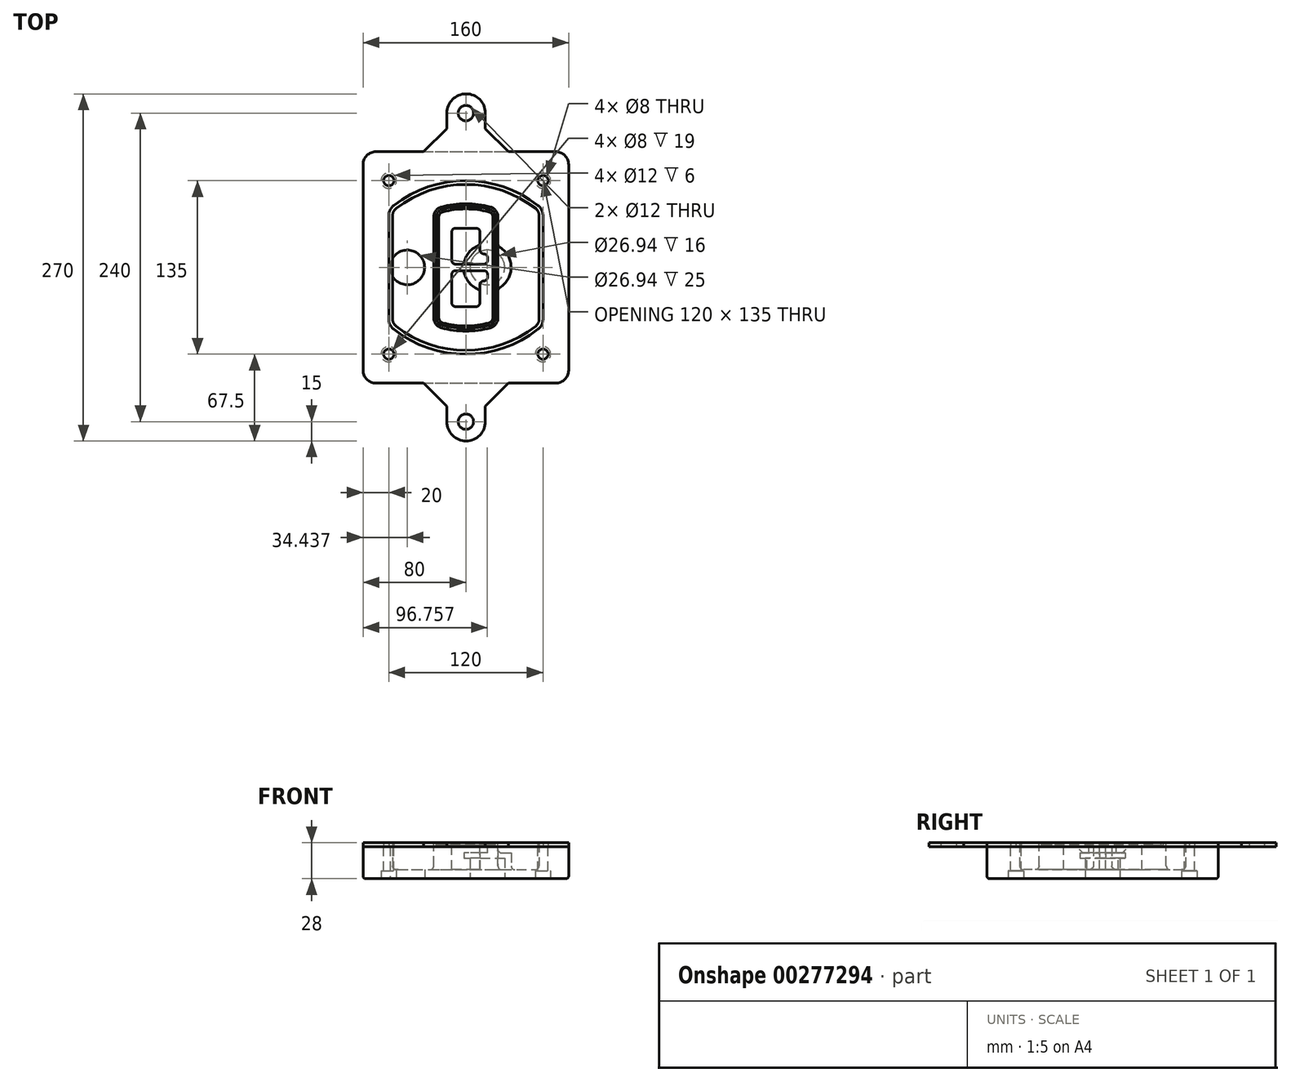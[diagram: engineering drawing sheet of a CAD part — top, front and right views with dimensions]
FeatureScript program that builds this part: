
annotation { "Feature Type Name" : "Feature", "Feature Type Description" : "" }
export const myFeature = defineFeature(function(context is Context, id is Id, definition is map)
    precondition{}
    {
        {
            var Q0;
            Q0=qCreatedBy(makeId("Top.planeOp"),FACE);
            var sketch = newSketch(context, id + "F0", { "sketchPlane" : qUnion([Q0])});
            skPoint(sketch, "E0.rect.middle", {"position": v(0, 0) * mm});
            skLineSegment(sketch, "E1.bottom", {"start": v(-70, -90) * mm, "end": v(70, -90) * mm});
            skLineSegment(sketch, "E1.top", {"start": v(-70, 90) * mm, "end": v(70, 90) * mm});
            skLineSegment(sketch, "E1.left", {"start": v(-80, -80) * mm, "end": v(-80, 80) * mm});
            skLineSegment(sketch, "E1.right", {"start": v(80, -80) * mm, "end": v(80, 80) * mm});
            skLineSegment(sketch, "E2", {"start": v(-80, 90) * mm, "end": v(80, -90) * mm, "construction": true});
            skLineSegment(sketch, "E3", {"start": v(80, 90) * mm, "end": v(-80, -90) * mm, "construction": true});
            skCircle(sketch, "E4", {"center": v(-60, 67.5) * mm, "radius": 4 * mm});
            skCircle(sketch, "E5", {"center": v(60, 67.5) * mm, "radius": 4 * mm});
            skCircle(sketch, "E6", {"center": v(60, -67.5) * mm, "radius": 4 * mm});
            skCircle(sketch, "E7", {"center": v(-60, -67.5) * mm, "radius": 4 * mm});
            skLineSegment(sketch, "E8", {"start": v(-60, 67.5) * mm, "end": v(60, 67.5) * mm, "construction": true});
            skLineSegment(sketch, "E9", {"start": v(60, 67.5) * mm, "end": v(60, -67.5) * mm, "construction": true});
            skLineSegment(sketch, "E10", {"start": v(60, -67.5) * mm, "end": v(-60, -67.5) * mm, "construction": true});
            skLineSegment(sketch, "E11", {"start": v(-60, -67.5) * mm, "end": v(-60, 67.5) * mm, "construction": true});
            skLineSegment(sketch, "E12", {"start": v(-60, 40.3) * mm, "end": v(-60, -40.3) * mm});
            skLineSegment(sketch, "E13", {"start": v(60, 40.3) * mm, "end": v(60, -40.3) * mm});
            skArc(sketch, "E14", {"start": v(56.15, 48.18) * mm, "mid": v(0, 67.5) * mm, "end": v(-56.15, 48.18) * mm});
            skArc(sketch, "E15", {"start": v(-56.15, -48.18) * mm, "mid": v(0, -67.5) * mm, "end": v(56.15, -48.18) * mm});
            skLineSegment(sketch, "E16", {"start": v(-60, 0) * mm, "end": v(60, 0) * mm, "construction": true});
            skPoint(sketch, "E17.visualSharp", {"position": v(-60, -45) * mm});
            skArc(sketch, "E17.filletArc", {"start": v(-60, -40.3) * mm, "mid": v(-58.99, -44.68) * mm, "end": v(-56.15, -48.18) * mm});
            skPoint(sketch, "E18.visualSharp", {"position": v(-60, 45) * mm});
            skArc(sketch, "E18.filletArc", {"start": v(-56.15, 48.18) * mm, "mid": v(-58.99, 44.68) * mm, "end": v(-60, 40.3) * mm});
            skPoint(sketch, "E19.visualSharp", {"position": v(60, 45) * mm});
            skArc(sketch, "E19.filletArc", {"start": v(60, 40.3) * mm, "mid": v(58.99, 44.68) * mm, "end": v(56.15, 48.18) * mm});
            skPoint(sketch, "E20.visualSharp", {"position": v(60, -45) * mm});
            skArc(sketch, "E20.filletArc", {"start": v(56.15, -48.18) * mm, "mid": v(58.99, -44.68) * mm, "end": v(60, -40.3) * mm});
            skPoint(sketch, "E21.visualSharp", {"position": v(-80, 90) * mm});
            skArc(sketch, "E21.filletArc", {"start": v(-70, 90) * mm, "mid": v(-77.07, 87.07) * mm, "end": v(-80, 80) * mm});
            skPoint(sketch, "E22.visualSharp", {"position": v(80, 90) * mm});
            skArc(sketch, "E22.filletArc", {"start": v(80, 80) * mm, "mid": v(77.07, 87.07) * mm, "end": v(70, 90) * mm});
            skPoint(sketch, "E23.visualSharp", {"position": v(80, -90) * mm});
            skArc(sketch, "E23.filletArc", {"start": v(70, -90) * mm, "mid": v(77.07, -87.07) * mm, "end": v(80, -80) * mm});
            skPoint(sketch, "E24.visualSharp", {"position": v(-80, -90) * mm});
            skArc(sketch, "E24.filletArc", {"start": v(-80, -80) * mm, "mid": v(-77.07, -87.07) * mm, "end": v(-70, -90) * mm});
            skArc(sketch, "E25.0", {"start": v(57, 40.3) * mm, "mid": v(56.3, 43.36) * mm, "end": v(54.3, 45.81) * mm});
            skLineSegment(sketch, "E25.1", {"start": v(57, 40.3) * mm, "end": v(57, -40.3) * mm});
            skArc(sketch, "E25.2", {"start": v(54.3, -45.81) * mm, "mid": v(56.3, -43.36) * mm, "end": v(57, -40.3) * mm});
            skArc(sketch, "E25.3", {"start": v(-54.3, -45.81) * mm, "mid": v(0, -64.5) * mm, "end": v(54.3, -45.81) * mm});
            skArc(sketch, "E25.4", {"start": v(-57, -40.3) * mm, "mid": v(-56.3, -43.36) * mm, "end": v(-54.3, -45.81) * mm});
            skArc(sketch, "E25.5", {"start": v(54.3, 45.81) * mm, "mid": v(0, 64.5) * mm, "end": v(-54.3, 45.81) * mm});
            skLineSegment(sketch, "E25.6", {"start": v(-57, 40.3) * mm, "end": v(-57, -40.3) * mm});
            skArc(sketch, "E25.7", {"start": v(-54.3, 45.81) * mm, "mid": v(-56.3, 43.36) * mm, "end": v(-57, 40.3) * mm});
            skArc(sketch, "E26.0", {"start": v(-58.62, 51.33) * mm, "mid": v(-62.58, 46.43) * mm, "end": v(-64, 40.3) * mm});
            skArc(sketch, "E26.1", {"start": v(58.62, 51.33) * mm, "mid": v(0, 71.5) * mm, "end": v(-58.62, 51.33) * mm});
            skArc(sketch, "E26.2", {"start": v(64, 40.3) * mm, "mid": v(62.58, 46.43) * mm, "end": v(58.62, 51.33) * mm});
            skLineSegment(sketch, "E26.3", {"start": v(64, 40.3) * mm, "end": v(64, -40.3) * mm});
            skArc(sketch, "E26.4", {"start": v(58.62, -51.33) * mm, "mid": v(62.58, -46.43) * mm, "end": v(64, -40.3) * mm});
            skLineSegment(sketch, "E26.5", {"start": v(-64, 40.3) * mm, "end": v(-64, -40.3) * mm});
            skArc(sketch, "E26.6", {"start": v(-58.62, -51.33) * mm, "mid": v(0, -71.5) * mm, "end": v(58.62, -51.33) * mm});
            skArc(sketch, "E26.7", {"start": v(-64, -40.3) * mm, "mid": v(-62.58, -46.43) * mm, "end": v(-58.62, -51.33) * mm});
            skSolve(sketch);
        }
        {
            var Q0;
            Q0=makeQuery(id+"F0.imprint","IMPRINT",FACE,{"disambiguationData":[TD([[makeQuery(id+"F0.imprint","IMPRINT",EDGE,{"derivedFrom":sQuery(id+"F0.wireOp",EDGE,"E1.bottom")}),1.0]])]});
            var Q1;
            Q1=makeQuery(id+"F0.imprint","IMPRINT",FACE,{"disambiguationData":[TD([[makeQuery(id+"F0.imprint","IMPRINT",EDGE,{"derivedFrom":sQuery(id+"F0.wireOp",EDGE,"E12")}),1.0]])]});
            var Q2;
            Q2=makeQuery(id+"F0.imprint","IMPRINT",FACE,{"disambiguationData":[TD([[makeQuery(id+"F0.imprint","IMPRINT",EDGE,{"derivedFrom":sQuery(id+"F0.wireOp",EDGE,"E25.0")}),1.0]])]});
            var Q3;
            Q3=makeQuery(id+"F0.imprint","IMPRINT",FACE,{"disambiguationData":[TD([[makeQuery(id+"F0.imprint","IMPRINT",EDGE,{"derivedFrom":sQuery(id+"F0.wireOp",EDGE,"E12")}),-1.0]])]});
            extrude(context, id + "F1", {"entities" : qUnion([Q0, Q1, Q2, Q3]), "oppositeDirection" : true, "depth" : 25 * mm});
        }
        {
            var Q0;
            Q0=makeQuery(id+"F0.imprint","IMPRINT",FACE,{"disambiguationData":[TD([[makeQuery(id+"F0.imprint","IMPRINT",EDGE,{"derivedFrom":sQuery(id+"F0.wireOp",EDGE,"E12")}),1.0]])]});
            extrude(context, id + "F2", {"entities" : qUnion([Q0]), "operationType" : NewBodyOperationType.ADD, "depth" : 3 * mm});
        }
        {
            var Q0;
            Q0=makeQuery(id+"F0.imprint","IMPRINT",FACE,{"disambiguationData":[TD([[makeQuery(id+"F0.imprint","IMPRINT",EDGE,{"derivedFrom":sQuery(id+"F0.wireOp",EDGE,"E25.0")}),1.0]])]});
            extrude(context, id + "F3", {"entities" : qUnion([Q0]), "operationType" : NewBodyOperationType.REMOVE, "oppositeDirection" : true, "depth" : 18 * mm});
        }
        {
            var Q0;
            Q0=makeQuery(id+"F2.opExtrude","CAP_FACE",FACE,{"disambiguationData":[OSD([sQuery(id+"F0.wireOp",EDGE,"E12"),sQuery(id+"F0.wireOp",EDGE,"E13"),sQuery(id+"F0.wireOp",EDGE,"E14"),sQuery(id+"F0.wireOp",EDGE,"E15"),sQuery(id+"F0.wireOp",EDGE,"E17.filletArc"),sQuery(id+"F0.wireOp",EDGE,"E18.filletArc"),sQuery(id+"F0.wireOp",EDGE,"E19.filletArc"),sQuery(id+"F0.wireOp",EDGE,"E20.filletArc"),sQuery(id+"F0.wireOp",EDGE,"E25.0"),sQuery(id+"F0.wireOp",EDGE,"E25.1"),sQuery(id+"F0.wireOp",EDGE,"E25.2"),sQuery(id+"F0.wireOp",EDGE,"E25.3"),sQuery(id+"F0.wireOp",EDGE,"E25.4"),sQuery(id+"F0.wireOp",EDGE,"E25.5"),sQuery(id+"F0.wireOp",EDGE,"E25.6"),sQuery(id+"F0.wireOp",EDGE,"E25.7")])],"isStart":false});
            var sketch = newSketch(context, id + "F4", { "sketchPlane" : qUnion([Q0])});
            skArc(sketch, "E27.0", {"start": v(-19.08, -46.97) * mm, "mid": v(0, -49.5) * mm, "end": v(19.08, -46.97) * mm});
            skArc(sketch, "E28.0", {"start": v(19.08, 46.97) * mm, "mid": v(0, 49.5) * mm, "end": v(-19.08, 46.97) * mm});
            skLineSegment(sketch, "E29", {"start": v(-25, 39.25) * mm, "end": v(-25, -39.25) * mm});
            skLineSegment(sketch, "E30", {"start": v(25, 39.25) * mm, "end": v(25, -39.25) * mm});
            skLineSegment(sketch, "E31", {"start": v(-25, 45.1) * mm, "end": v(25, 45.1) * mm, "construction": true});
            skLineSegment(sketch, "E32", {"start": v(-25, -45.1) * mm, "end": v(25, -45.1) * mm, "construction": true});
            skPoint(sketch, "E33.visualSharp", {"position": v(-25, 45.1) * mm});
            skArc(sketch, "E33.filletArc", {"start": v(-19.08, 46.97) * mm, "mid": v(-23.35, 44.11) * mm, "end": v(-25, 39.25) * mm});
            skPoint(sketch, "E34.visualSharp", {"position": v(25, 45.1) * mm});
            skArc(sketch, "E34.filletArc", {"start": v(25, 39.25) * mm, "mid": v(23.35, 44.11) * mm, "end": v(19.08, 46.97) * mm});
            skPoint(sketch, "E35.visualSharp", {"position": v(25, -45.1) * mm});
            skArc(sketch, "E35.filletArc", {"start": v(19.08, -46.97) * mm, "mid": v(23.35, -44.11) * mm, "end": v(25, -39.25) * mm});
            skPoint(sketch, "E36.visualSharp", {"position": v(-25, -45.1) * mm});
            skArc(sketch, "E36.filletArc", {"start": v(-25, -39.25) * mm, "mid": v(-23.35, -44.11) * mm, "end": v(-19.08, -46.97) * mm});
            skArc(sketch, "E37.0", {"start": v(54.3, 45.81) * mm, "mid": v(0, 64.5) * mm, "end": v(-54.3, 45.81) * mm});
            skArc(sketch, "E37.1", {"start": v(-54.3, 45.81) * mm, "mid": v(-56.3, 43.36) * mm, "end": v(-57, 40.3) * mm});
            skLineSegment(sketch, "E37.2", {"start": v(-57, 40.3) * mm, "end": v(-57, -40.3) * mm});
            skArc(sketch, "E37.3", {"start": v(-57, -40.3) * mm, "mid": v(-56.3, -43.36) * mm, "end": v(-54.3, -45.81) * mm});
            skArc(sketch, "E37.4", {"start": v(-54.3, -45.81) * mm, "mid": v(0, -64.5) * mm, "end": v(54.3, -45.81) * mm});
            skArc(sketch, "E37.5", {"start": v(54.3, -45.81) * mm, "mid": v(56.3, -43.36) * mm, "end": v(57, -40.3) * mm});
            skLineSegment(sketch, "E37.6", {"start": v(57, 40.3) * mm, "end": v(57, -40.3) * mm});
            skArc(sketch, "E37.7", {"start": v(57, 40.3) * mm, "mid": v(56.3, 43.36) * mm, "end": v(54.3, 45.81) * mm});
            skLineSegment(sketch, "E38.0", {"start": v(23, 39.25) * mm, "end": v(23, -39.25) * mm});
            skArc(sketch, "E38.1", {"start": v(18.56, -45.04) * mm, "mid": v(21.76, -42.9) * mm, "end": v(23, -39.25) * mm});
            skArc(sketch, "E38.2", {"start": v(-18.56, -45.04) * mm, "mid": v(0, -47.5) * mm, "end": v(18.56, -45.04) * mm});
            skArc(sketch, "E38.3", {"start": v(-23, -39.25) * mm, "mid": v(-21.76, -42.9) * mm, "end": v(-18.56, -45.04) * mm});
            skLineSegment(sketch, "E38.4", {"start": v(-23, 39.25) * mm, "end": v(-23, -39.25) * mm});
            skArc(sketch, "E38.5", {"start": v(23, 39.25) * mm, "mid": v(21.76, 42.9) * mm, "end": v(18.56, 45.04) * mm});
            skArc(sketch, "E38.6", {"start": v(-18.56, 45.04) * mm, "mid": v(-21.76, 42.9) * mm, "end": v(-23, 39.25) * mm});
            skArc(sketch, "E38.7", {"start": v(18.56, 45.04) * mm, "mid": v(0, 47.5) * mm, "end": v(-18.56, 45.04) * mm});
            skArc(sketch, "E39.0", {"start": v(21, 39.25) * mm, "mid": v(20.18, 41.68) * mm, "end": v(18.04, 43.1) * mm});
            skLineSegment(sketch, "E39.1", {"start": v(21, 39.25) * mm, "end": v(21, -39.25) * mm});
            skArc(sketch, "E39.2", {"start": v(18.04, -43.1) * mm, "mid": v(20.18, -41.68) * mm, "end": v(21, -39.25) * mm});
            skArc(sketch, "E39.3", {"start": v(-18.04, -43.1) * mm, "mid": v(0, -45.5) * mm, "end": v(18.04, -43.1) * mm});
            skArc(sketch, "E39.4", {"start": v(-21, -39.25) * mm, "mid": v(-20.18, -41.68) * mm, "end": v(-18.04, -43.1) * mm});
            skArc(sketch, "E39.5", {"start": v(18.04, 43.1) * mm, "mid": v(0, 45.5) * mm, "end": v(-18.04, 43.1) * mm});
            skLineSegment(sketch, "E39.6", {"start": v(-21, 39.25) * mm, "end": v(-21, -39.25) * mm});
            skArc(sketch, "E39.7", {"start": v(-18.04, 43.1) * mm, "mid": v(-20.18, 41.68) * mm, "end": v(-21, 39.25) * mm});
            skLineSegment(sketch, "E40", {"start": v(-25, 0) * mm, "end": v(25, 0) * mm, "construction": true});
            skLineSegment(sketch, "E41", {"start": v(-11, 5.5) * mm, "end": v(-11, 27.5) * mm});
            skLineSegment(sketch, "E42", {"start": v(-8, 30.5) * mm, "end": v(8, 30.5) * mm});
            skLineSegment(sketch, "E43", {"start": v(11, 27.5) * mm, "end": v(11, 13.5) * mm});
            skLineSegment(sketch, "E44", {"start": v(14, 10.5) * mm, "end": v(14, 10.5) * mm});
            skLineSegment(sketch, "E45", {"start": v(17, 7.5) * mm, "end": v(17, 5.5) * mm});
            skLineSegment(sketch, "E46", {"start": v(14, 2.5) * mm, "end": v(-8, 2.5) * mm});
            skPoint(sketch, "E47.visualSharp", {"position": v(-11, 30.5) * mm});
            skArc(sketch, "E47.filletArc", {"start": v(-8, 30.5) * mm, "mid": v(-10.12, 29.62) * mm, "end": v(-11, 27.5) * mm});
            skPoint(sketch, "E48.visualSharp", {"position": v(11, 30.5) * mm});
            skArc(sketch, "E48.filletArc", {"start": v(11, 27.5) * mm, "mid": v(10.12, 29.62) * mm, "end": v(8, 30.5) * mm});
            skPoint(sketch, "E49.visualSharp", {"position": v(11, 10.5) * mm});
            skArc(sketch, "E49.filletArc", {"start": v(11, 13.5) * mm, "mid": v(11.88, 11.38) * mm, "end": v(14, 10.5) * mm});
            skPoint(sketch, "E50.visualSharp", {"position": v(17, 10.5) * mm});
            skArc(sketch, "E50.filletArc", {"start": v(17, 7.5) * mm, "mid": v(16.12, 9.62) * mm, "end": v(14, 10.5) * mm});
            skPoint(sketch, "E51.visualSharp", {"position": v(17, 2.5) * mm});
            skArc(sketch, "E51.filletArc", {"start": v(14, 2.5) * mm, "mid": v(16.12, 3.38) * mm, "end": v(17, 5.5) * mm});
            skPoint(sketch, "E52.visualSharp", {"position": v(-11, 2.5) * mm});
            skArc(sketch, "E52.filletArc", {"start": v(-11, 5.5) * mm, "mid": v(-10.12, 3.38) * mm, "end": v(-8, 2.5) * mm});
            skLineSegment(sketch, "E53.0.MirrorCS", {"start": v(14, -2.5) * mm, "end": v(-8, -2.5) * mm});
            skArc(sketch, "E54.0.MirrorCS", {"start": v(-11, -5.5) * mm, "mid": v(-10.12, -3.38) * mm, "end": v(-8, -2.5) * mm});
            skLineSegment(sketch, "E55.0.MirrorCS", {"start": v(-11, -5.5) * mm, "end": v(-11, -27.5) * mm});
            skArc(sketch, "E56.0.MirrorCS", {"start": v(-8, -30.5) * mm, "mid": v(-10.12, -29.62) * mm, "end": v(-11, -27.5) * mm});
            skLineSegment(sketch, "E57.0.MirrorCS", {"start": v(-8, -30.5) * mm, "end": v(8, -30.5) * mm});
            skArc(sketch, "E58.0.MirrorCS", {"start": v(11, -27.5) * mm, "mid": v(10.12, -29.62) * mm, "end": v(8, -30.5) * mm});
            skLineSegment(sketch, "E59.0.MirrorCS", {"start": v(11, -27.5) * mm, "end": v(11, -13.5) * mm});
            skArc(sketch, "E60.0.MirrorCS", {"start": v(11, -13.5) * mm, "mid": v(11.88, -11.38) * mm, "end": v(14, -10.5) * mm});
            skArc(sketch, "E61.0.MirrorCS", {"start": v(17, -7.5) * mm, "mid": v(16.12, -9.62) * mm, "end": v(14, -10.5) * mm});
            skLineSegment(sketch, "E62.0.MirrorCS", {"start": v(17, -7.5) * mm, "end": v(17, -5.5) * mm});
            skArc(sketch, "E63.0.MirrorCS", {"start": v(14, -2.5) * mm, "mid": v(16.12, -3.38) * mm, "end": v(17, -5.5) * mm});
            skSolve(sketch);
        }
        {
            var Q0;
            Q0=makeQuery(id+"F4.imprint","IMPRINT",FACE,{"disambiguationData":[TD([[makeQuery(id+"F4.imprint","IMPRINT",EDGE,{"derivedFrom":sQuery(id+"F4.wireOp",EDGE,"E27.0")}),1.0]])]});
            var Q1;
            Q1=makeQuery(id+"F4.imprint","IMPRINT",FACE,{"disambiguationData":[TD([[makeQuery(id+"F4.imprint","IMPRINT",EDGE,{"derivedFrom":sQuery(id+"F4.wireOp",EDGE,"E38.0")}),-1.0]])]});
            var Q2;
            Q2=makeQuery(id+"F4.imprint","IMPRINT",FACE,{"disambiguationData":[TD([[makeQuery(id+"F4.imprint","IMPRINT",EDGE,{"derivedFrom":sQuery(id+"F4.wireOp",EDGE,"E39.0")}),1.0]])]});
            extrude(context, id + "F5", {"entities" : qUnion([Q0, Q1, Q2]), "operationType" : NewBodyOperationType.ADD, "endBound" : BoundingType.UP_TO_NEXT, "oppositeDirection" : true, "depth" : 25 * mm});
        }
        {
            var Q0;
            Q0=makeQuery(id+"F4.imprint","IMPRINT",FACE,{"disambiguationData":[TD([[makeQuery(id+"F4.imprint","IMPRINT",EDGE,{"derivedFrom":sQuery(id+"F4.wireOp",EDGE,"E38.0")}),-1.0]])]});
            extrude(context, id + "F6", {"entities" : qUnion([Q0]), "operationType" : NewBodyOperationType.REMOVE, "oppositeDirection" : true, "depth" : 2 * mm});
        }
        {
            var Q0;
            Q0=makeQuery(id+"F1.opExtrude","CAP_FACE",FACE,{"disambiguationData":[OSD([sQuery(id+"F0.wireOp",EDGE,"E1.bottom"),sQuery(id+"F0.wireOp",EDGE,"E1.top"),sQuery(id+"F0.wireOp",EDGE,"E1.left"),sQuery(id+"F0.wireOp",EDGE,"E1.right"),sQuery(id+"F0.wireOp",EDGE,"E4"),sQuery(id+"F0.wireOp",EDGE,"E5"),sQuery(id+"F0.wireOp",EDGE,"E6"),sQuery(id+"F0.wireOp",EDGE,"E7"),sQuery(id+"F0.wireOp",EDGE,"E21.filletArc"),sQuery(id+"F0.wireOp",EDGE,"E22.filletArc"),sQuery(id+"F0.wireOp",EDGE,"E23.filletArc"),sQuery(id+"F0.wireOp",EDGE,"E24.filletArc")])],"isStart":false});
            var sketch = newSketch(context, id + "F7", { "sketchPlane" : qUnion([Q0])});
            skCircle(sketch, "E64", {"center": v(16.76, 0) * mm, "radius": 13.47 * mm});
            skCircle(sketch, "E65", {"center": v(-45.56, 0) * mm, "radius": 13.47 * mm});
            skLineSegment(sketch, "E66", {"start": v(80, 0) * mm, "end": v(-80, 0) * mm});
            skCircle(sketch, "E67", {"center": v(16.76, 0) * mm, "radius": 18.47 * mm});
            skCircle(sketch, "E68", {"center": v(60, -67.5) * mm, "radius": 6 * mm});
            skCircle(sketch, "E69", {"center": v(-60, -67.5) * mm, "radius": 6 * mm});
            skCircle(sketch, "E70", {"center": v(-60, 67.5) * mm, "radius": 6 * mm});
            skCircle(sketch, "E71", {"center": v(60, 67.5) * mm, "radius": 6 * mm});
            skSolve(sketch);
        }
        {
            var Q0;
            {var subQ1=sQuery(id+"F7.wireOp",EDGE,"E66");var subQ4=sQuery(id+"F7.wireOp",EDGE,"E64");var subQ6=makeQuery(id+"F7.imprint","INTERSECT",VERTEX,{"disambiguationData":[OD(0.0)],"derivedFrom":[subQ4,subQ1]});Q0=makeQuery(id+"F7.imprint","IMPRINT",FACE,{"disambiguationData":[TD([[makeQuery(id+"F7.imprint","IMPRINT",EDGE,{"disambiguationData":[TD([[subQ6,-1.0]])],"derivedFrom":subQ4}),-1.0]])]});}
            var Q1;
            {var subQ0=sQuery(id+"F7.wireOp",EDGE,"E66");var subQ1=sQuery(id+"F7.wireOp",EDGE,"E64");var subQ3=makeQuery(id+"F7.imprint","INTERSECT",VERTEX,{"disambiguationData":[OD(0.0)],"derivedFrom":[subQ1,subQ0]});Q1=makeQuery(id+"F7.imprint","IMPRINT",FACE,{"disambiguationData":[TD([[makeQuery(id+"F7.imprint","IMPRINT",EDGE,{"disambiguationData":[TD([[subQ3,-1.0]])],"derivedFrom":subQ1}),1.0]])]});}
            var Q2;
            {var subQ0=sQuery(id+"F7.wireOp",EDGE,"E66");var subQ1=sQuery(id+"F7.wireOp",EDGE,"E64");var subQ3=makeQuery(id+"F7.imprint","INTERSECT",VERTEX,{"disambiguationData":[OD(0.0)],"derivedFrom":[subQ1,subQ0]});Q2=makeQuery(id+"F7.imprint","IMPRINT",FACE,{"disambiguationData":[TD([[makeQuery(id+"F7.imprint","IMPRINT",EDGE,{"disambiguationData":[TD([[subQ3,1.0]])],"derivedFrom":subQ1}),1.0]])]});}
            var Q3;
            {var subQ1=sQuery(id+"F7.wireOp",EDGE,"E66");var subQ4=sQuery(id+"F7.wireOp",EDGE,"E64");var subQ6=makeQuery(id+"F7.imprint","INTERSECT",VERTEX,{"disambiguationData":[OD(0.0)],"derivedFrom":[subQ4,subQ1]});Q3=makeQuery(id+"F7.imprint","IMPRINT",FACE,{"disambiguationData":[TD([[makeQuery(id+"F7.imprint","IMPRINT",EDGE,{"disambiguationData":[TD([[subQ6,1.0]])],"derivedFrom":subQ4}),-1.0]])]});}
            extrude(context, id + "F8", {"entities" : qUnion([Q0, Q1, Q2, Q3]), "operationType" : NewBodyOperationType.ADD, "oppositeDirection" : true, "depth" : 20 * mm});
        }
        {
            var Q0;
            {var subQ0=sQuery(id+"F7.wireOp",EDGE,"E66");var subQ1=sQuery(id+"F7.wireOp",EDGE,"E64");var subQ3=makeQuery(id+"F7.imprint","INTERSECT",VERTEX,{"disambiguationData":[OD(0.0)],"derivedFrom":[subQ1,subQ0]});Q0=makeQuery(id+"F7.imprint","IMPRINT",FACE,{"disambiguationData":[TD([[makeQuery(id+"F7.imprint","IMPRINT",EDGE,{"disambiguationData":[TD([[subQ3,-1.0]])],"derivedFrom":subQ1}),1.0]])]});}
            var Q1;
            {var subQ0=sQuery(id+"F7.wireOp",EDGE,"E66");var subQ1=sQuery(id+"F7.wireOp",EDGE,"E64");var subQ3=makeQuery(id+"F7.imprint","INTERSECT",VERTEX,{"disambiguationData":[OD(0.0)],"derivedFrom":[subQ1,subQ0]});Q1=makeQuery(id+"F7.imprint","IMPRINT",FACE,{"disambiguationData":[TD([[makeQuery(id+"F7.imprint","IMPRINT",EDGE,{"disambiguationData":[TD([[subQ3,1.0]])],"derivedFrom":subQ1}),1.0]])]});}
            extrude(context, id + "F9", {"entities" : qUnion([Q0, Q1]), "operationType" : NewBodyOperationType.REMOVE, "oppositeDirection" : true, "depth" : 16 * mm});
        }
        {
            var Q0;
            {var subQ0=sQuery(id+"F7.wireOp",EDGE,"E66");var subQ1=sQuery(id+"F7.wireOp",EDGE,"E65");var subQ3=makeQuery(id+"F7.imprint","INTERSECT",VERTEX,{"disambiguationData":[OD(0.0)],"derivedFrom":[subQ1,subQ0]});Q0=makeQuery(id+"F7.imprint","IMPRINT",FACE,{"disambiguationData":[TD([[makeQuery(id+"F7.imprint","IMPRINT",EDGE,{"disambiguationData":[TD([[subQ3,-1.0]])],"derivedFrom":subQ1}),1.0]])]});}
            var Q1;
            {var subQ0=sQuery(id+"F7.wireOp",EDGE,"E66");var subQ1=sQuery(id+"F7.wireOp",EDGE,"E65");var subQ3=makeQuery(id+"F7.imprint","INTERSECT",VERTEX,{"disambiguationData":[OD(0.0)],"derivedFrom":[subQ1,subQ0]});Q1=makeQuery(id+"F7.imprint","IMPRINT",FACE,{"disambiguationData":[TD([[makeQuery(id+"F7.imprint","IMPRINT",EDGE,{"disambiguationData":[TD([[subQ3,1.0]])],"derivedFrom":subQ1}),1.0]])]});}
            extrude(context, id + "F10", {"entities" : qUnion([Q0, Q1]), "operationType" : NewBodyOperationType.REMOVE, "oppositeDirection" : true, "depth" : 25 * mm});
        }
        {
            var Q0;
            Q0=makeQuery(id+"F7.imprint","IMPRINT",FACE,{"disambiguationData":[TD([[makeQuery(id+"F7.imprint","IMPRINT",EDGE,{"derivedFrom":sQuery(id+"F7.wireOp",EDGE,"E68")}),1.0]])]});
            var Q1;
            Q1=makeQuery(id+"F7.imprint","IMPRINT",FACE,{"disambiguationData":[TD([[makeQuery(id+"F7.imprint","IMPRINT",EDGE,{"derivedFrom":makeQuery(id+"F1.opExtrude","CAP_EDGE",EDGE,{"disambiguationData":[OSD([sQuery(id+"F0.wireOp",EDGE,"E5")])],"isStart":false})}),-1.0]])]});
            var Q2;
            Q2=makeQuery(id+"F7.imprint","IMPRINT",FACE,{"disambiguationData":[TD([[makeQuery(id+"F7.imprint","IMPRINT",EDGE,{"derivedFrom":sQuery(id+"F7.wireOp",EDGE,"E69")}),1.0]])]});
            var Q3;
            Q3=makeQuery(id+"F7.imprint","IMPRINT",FACE,{"disambiguationData":[TD([[makeQuery(id+"F7.imprint","IMPRINT",EDGE,{"derivedFrom":makeQuery(id+"F1.opExtrude","CAP_EDGE",EDGE,{"disambiguationData":[OSD([sQuery(id+"F0.wireOp",EDGE,"E4")])],"isStart":false})}),-1.0]])]});
            var Q4;
            Q4=makeQuery(id+"F7.imprint","IMPRINT",FACE,{"disambiguationData":[TD([[makeQuery(id+"F7.imprint","IMPRINT",EDGE,{"derivedFrom":sQuery(id+"F7.wireOp",EDGE,"E70")}),1.0]])]});
            var Q5;
            Q5=makeQuery(id+"F7.imprint","IMPRINT",FACE,{"disambiguationData":[TD([[makeQuery(id+"F7.imprint","IMPRINT",EDGE,{"derivedFrom":makeQuery(id+"F1.opExtrude","CAP_EDGE",EDGE,{"disambiguationData":[OSD([sQuery(id+"F0.wireOp",EDGE,"E7")])],"isStart":false})}),-1.0]])]});
            var Q6;
            Q6=makeQuery(id+"F7.imprint","IMPRINT",FACE,{"disambiguationData":[TD([[makeQuery(id+"F7.imprint","IMPRINT",EDGE,{"derivedFrom":sQuery(id+"F7.wireOp",EDGE,"E71")}),1.0]])]});
            var Q7;
            Q7=makeQuery(id+"F7.imprint","IMPRINT",FACE,{"disambiguationData":[TD([[makeQuery(id+"F7.imprint","IMPRINT",EDGE,{"derivedFrom":makeQuery(id+"F1.opExtrude","CAP_EDGE",EDGE,{"disambiguationData":[OSD([sQuery(id+"F0.wireOp",EDGE,"E6")])],"isStart":false})}),-1.0]])]});
            extrude(context, id + "F11", {"entities" : qUnion([Q0, Q1, Q2, Q3, Q4, Q5, Q6, Q7]), "operationType" : NewBodyOperationType.REMOVE, "oppositeDirection" : true, "depth" : 6 * mm});
        }
        {
            var Q0;
            Q0=makeQuery(id+"F9.boolean.opBoolean","COPY",FACE,{"derivedFrom":makeQuery(id+"F9.opExtrude","CAP_FACE",FACE,{"disambiguationData":[OSD([sQuery(id+"F7.wireOp",EDGE,"E64")])],"isStart":false})});
            var sketch = newSketch(context, id + "F12", { "sketchPlane" : qUnion([Q0])});
            skArc(sketch, "E72.0", {"start": v(11, 17.55) * mm, "mid": v(2.57, 11.82) * mm, "end": v(-1.54, 2.5) * mm});
            skArc(sketch, "E72.1", {"start": v(-1.54, -2.5) * mm, "mid": v(2.57, -11.82) * mm, "end": v(11, -17.55) * mm});
            skLineSegment(sketch, "E73", {"start": v(-1.54, -2.5) * mm, "end": v(14, -2.5) * mm});
            skLineSegment(sketch, "E74.0", {"start": v(14, 2.5) * mm, "end": v(-1.54, 2.5) * mm});
            skArc(sketch, "E74.1", {"start": v(14, 2.5) * mm, "mid": v(16.12, 3.38) * mm, "end": v(17, 5.5) * mm});
            skLineSegment(sketch, "E74.2", {"start": v(17, 7.5) * mm, "end": v(17, 5.5) * mm});
            skArc(sketch, "E74.3", {"start": v(17, 7.5) * mm, "mid": v(16.12, 9.62) * mm, "end": v(14, 10.5) * mm});
            skArc(sketch, "E74.4", {"start": v(11, 13.5) * mm, "mid": v(11.88, 11.38) * mm, "end": v(14, 10.5) * mm});
            skLineSegment(sketch, "E74.5", {"start": v(11, 17.55) * mm, "end": v(11, 13.5) * mm});
            skLineSegment(sketch, "E74.7", {"start": v(14, -2.5) * mm, "end": v(-1.54, -2.5) * mm});
            skArc(sketch, "E74.8", {"start": v(14, -2.5) * mm, "mid": v(16.12, -3.38) * mm, "end": v(17, -5.5) * mm});
            skLineSegment(sketch, "E74.9", {"start": v(17, -7.5) * mm, "end": v(17, -5.5) * mm});
            skArc(sketch, "E74.10", {"start": v(17, -7.5) * mm, "mid": v(16.12, -9.62) * mm, "end": v(14, -10.5) * mm});
            skArc(sketch, "E74.11", {"start": v(11, -13.5) * mm, "mid": v(11.88, -11.38) * mm, "end": v(14, -10.5) * mm});
            skLineSegment(sketch, "E74.12", {"start": v(11, -17.55) * mm, "end": v(11, -13.5) * mm});
            skPoint(sketch, "E75.orphan", {"position": v(11, -27.5) * mm});
            skPoint(sketch, "E76.orphan", {"position": v(-8, -2.5) * mm});
            skPoint(sketch, "E77.orphan", {"position": v(-8, 2.5) * mm});
            skPoint(sketch, "E78.orphan", {"position": v(11, 27.5) * mm});
            skSolve(sketch);
        }
        {
            var Q0;
            {var subQ7=sQuery(id+"F12.wireOp",EDGE,"E72.0");var subQ14=sQuery(id+"F12.wireOp",EDGE,"E72.1");var subQ16=sQuery(id+"F12.wireOp",EDGE,"E74.1");var subQ18=sQuery(id+"F12.wireOp",EDGE,"E74.8");Q0=qUnion([makeQuery(id+"F12.imprint","IMPRINT",FACE,{"disambiguationData":[TD([[makeQuery(id+"F12.imprint","IMPRINT",EDGE,{"derivedFrom":subQ7}),1.0]])]}),makeQuery(id+"F12.imprint","IMPRINT",FACE,{"disambiguationData":[TD([[makeQuery(id+"F12.imprint","IMPRINT",EDGE,{"derivedFrom":subQ14}),1.0]])]}),makeQuery(id+"F12.imprint","IMPRINT",FACE,{"disambiguationData":[TD([[makeQuery(id+"F12.imprint","IMPRINT",EDGE,{"derivedFrom":subQ16}),1.0]])]}),makeQuery(id+"F12.imprint","IMPRINT",FACE,{"disambiguationData":[TD([[makeQuery(id+"F12.imprint","IMPRINT",EDGE,{"derivedFrom":subQ18}),-1.0]])]})]);}
            var Q1;
            Q1=makeQuery(id+"F5.boolean.opBoolean","SPLIT",FACE,{"disambiguationData":[TD([makeQuery(id+"F5.opExtrude","SWEPT_FACE",FACE,{"disambiguationData":[OSD([sQuery(id+"F4.wireOp",EDGE,"E41")])]})])],"derivedFrom":makeQuery(id+"F3.boolean.opBoolean","COPY",FACE,{"derivedFrom":makeQuery(id+"F3.opExtrude","CAP_FACE",FACE,{"disambiguationData":[OSD([sQuery(id+"F0.wireOp",EDGE,"E25.0"),sQuery(id+"F0.wireOp",EDGE,"E25.1"),sQuery(id+"F0.wireOp",EDGE,"E25.2"),sQuery(id+"F0.wireOp",EDGE,"E25.3"),sQuery(id+"F0.wireOp",EDGE,"E25.4"),sQuery(id+"F0.wireOp",EDGE,"E25.5"),sQuery(id+"F0.wireOp",EDGE,"E25.6"),sQuery(id+"F0.wireOp",EDGE,"E25.7")])],"isStart":false})})});
            extrude(context, id + "F13", {"entities" : qUnion([Q0]), "operationType" : NewBodyOperationType.REMOVE, "endBound" : BoundingType.UP_TO_SURFACE, "endBoundEntityFace" : qUnion([Q1]), "depth" : 25 * mm});
        }
        {
            var Q0;
            Q0=makeQuery(id+"F3.boolean.opBoolean","COPY",EDGE,{"derivedFrom":makeQuery(id+"F3.opExtrude","CAP_EDGE",EDGE,{"disambiguationData":[OSD([sQuery(id+"F0.wireOp",EDGE,"E25.6")])],"isStart":false})});
            var Q1;
            Q1=makeQuery(id+"F8.boolean.opBoolean","INTERSECT",EDGE,{"derivedFrom":[makeQuery(id+"F5.opExtrude","SWEPT_FACE",FACE,{"disambiguationData":[OSD([sQuery(id+"F4.wireOp",EDGE,"E30")])]}),makeQuery(id+"F8.opExtrude","CAP_FACE",FACE,{"disambiguationData":[OSD([sQuery(id+"F7.wireOp",EDGE,"E67")])],"isStart":false})]});
            var Q2;
            Q2=makeQuery(id+"F8.boolean.opBoolean","INTERSECT",EDGE,{"disambiguationData":[OD(1.0)],"derivedFrom":[makeQuery(id+"F5.opExtrude","SWEPT_FACE",FACE,{"disambiguationData":[OSD([sQuery(id+"F4.wireOp",EDGE,"E30")])]}),makeQuery(id+"F8.opExtrude","SWEPT_FACE",FACE,{"disambiguationData":[OSD([sQuery(id+"F7.wireOp",EDGE,"E67")])]})]});
            var Q3;
            {var subQ0=sQuery(id+"F4.wireOp",EDGE,"E30");Q3=makeQuery(id+"F8.boolean.opBoolean","SPLIT",EDGE,{"disambiguationData":[TD([makeQuery(id+"F5.opExtrude","SWEPT_FACE",FACE,{"disambiguationData":[OSD([sQuery(id+"F4.wireOp",EDGE,"E35.filletArc")])]})])],"derivedFrom":makeQuery(id+"F5.opExtrude","CAP_EDGE",EDGE,{"disambiguationData":[OSD([subQ0])],"isStart":false})});}
            var Q4;
            {var subQ0=sQuery(id+"F0.wireOp",EDGE,"E25.7");var subQ1=sQuery(id+"F0.wireOp",EDGE,"E25.1");var subQ2=sQuery(id+"F0.wireOp",EDGE,"E25.6");var subQ3=sQuery(id+"F0.wireOp",EDGE,"E25.5");var subQ4=sQuery(id+"F0.wireOp",EDGE,"E25.4");var subQ5=sQuery(id+"F0.wireOp",EDGE,"E25.0");var subQ6=sQuery(id+"F0.wireOp",EDGE,"E25.2");var subQ7=sQuery(id+"F0.wireOp",EDGE,"E25.3");Q4=makeQuery(id+"F8.boolean.opBoolean","INTERSECT",EDGE,{"derivedFrom":[makeQuery(id+"F5.boolean.opBoolean","SPLIT",FACE,{"disambiguationData":[TD([makeQuery(id+"F2.opExtrude","SWEPT_FACE",FACE,{"disambiguationData":[OSD([subQ5])]})])],"derivedFrom":makeQuery(id+"F3.boolean.opBoolean","COPY",FACE,{"derivedFrom":makeQuery(id+"F3.opExtrude","CAP_FACE",FACE,{"disambiguationData":[OSD([subQ5,subQ1,subQ6,subQ7,subQ4,subQ3,subQ2,subQ0])],"isStart":false})})}),makeQuery(id+"F8.opExtrude","SWEPT_FACE",FACE,{"disambiguationData":[OSD([sQuery(id+"F7.wireOp",EDGE,"E67")])]})]});}
            var Q5;
            Q5=makeQuery(id+"F8.boolean.opBoolean","INTERSECT",EDGE,{"disambiguationData":[OD(0.0)],"derivedFrom":[makeQuery(id+"F5.opExtrude","SWEPT_FACE",FACE,{"disambiguationData":[OSD([sQuery(id+"F4.wireOp",EDGE,"E30")])]}),makeQuery(id+"F8.opExtrude","SWEPT_FACE",FACE,{"disambiguationData":[OSD([sQuery(id+"F7.wireOp",EDGE,"E67")])]})]});
            fillet(context, id + "F14", {"entities" : qUnion([Q0, Q1, Q2, Q3, Q4, Q5]), "radius" : 3 * mm, "tangentPropagation" : true, "allowEdgeOverflow" : false});
        }
        {
            var Q0;
            Q0=makeQuery(id+"F1.opExtrude","CAP_EDGE",EDGE,{"disambiguationData":[OSD([sQuery(id+"F0.wireOp",EDGE,"E1.bottom")])],"isStart":false});
            fillet(context, id + "F15", {"entities" : qUnion([Q0]), "radius" : 2 * mm, "tangentPropagation" : true, "allowEdgeOverflow" : false});
        }
        {
            var Q0;
            {var subQ0=sQuery(id+"F0.wireOp",EDGE,"E22.filletArc");var subQ1=sQuery(id+"F0.wireOp",EDGE,"E7");var subQ2=sQuery(id+"F0.wireOp",EDGE,"E6");var subQ3=sQuery(id+"F0.wireOp",EDGE,"E5");var subQ4=sQuery(id+"F0.wireOp",EDGE,"E4");var subQ5=sQuery(id+"F0.wireOp",EDGE,"E1.bottom");var subQ6=sQuery(id+"F0.wireOp",EDGE,"E21.filletArc");var subQ7=sQuery(id+"F0.wireOp",EDGE,"E1.top");var subQ8=sQuery(id+"F0.wireOp",EDGE,"E1.left");var subQ9=sQuery(id+"F0.wireOp",EDGE,"E1.right");var subQ10=sQuery(id+"F0.wireOp",EDGE,"E23.filletArc");var subQ11=sQuery(id+"F0.wireOp",EDGE,"E24.filletArc");Q0=makeQuery(id+"F2.boolean.opBoolean","SPLIT",FACE,{"disambiguationData":[TD([makeQuery(id+"F1.opExtrude","SWEPT_FACE",FACE,{"disambiguationData":[OSD([subQ5])]})])],"derivedFrom":makeQuery(id+"F1.opExtrude","CAP_FACE",FACE,{"disambiguationData":[OSD([subQ5,subQ7,subQ8,subQ9,subQ4,subQ3,subQ2,subQ1,subQ6,subQ0,subQ10,subQ11])],"isStart":true})});}
            var sketch = newSketch(context, id + "F16", { "sketchPlane" : qUnion([Q0])});
            skLineSegment(sketch, "E79.0", {"start": v(-70, 90) * mm, "end": v(70, 90) * mm});
            skArc(sketch, "E79.1", {"start": v(80, 80) * mm, "mid": v(77.07, 87.07) * mm, "end": v(70, 90) * mm});
            skLineSegment(sketch, "E79.2", {"start": v(80, -80) * mm, "end": v(80, 80) * mm});
            skArc(sketch, "E79.3", {"start": v(70, -90) * mm, "mid": v(77.07, -87.07) * mm, "end": v(80, -80) * mm});
            skLineSegment(sketch, "E79.4", {"start": v(-70, -90) * mm, "end": v(70, -90) * mm});
            skArc(sketch, "E79.5", {"start": v(-80, -80) * mm, "mid": v(-77.07, -87.07) * mm, "end": v(-70, -90) * mm});
            skLineSegment(sketch, "E79.6", {"start": v(-80, -80) * mm, "end": v(-80, 80) * mm});
            skArc(sketch, "E79.7", {"start": v(-70, 90) * mm, "mid": v(-77.07, 87.07) * mm, "end": v(-80, 80) * mm});
            skCircle(sketch, "E79.8", {"center": v(-60, 67.5) * mm, "radius": 4 * mm});
            skCircle(sketch, "E79.9", {"center": v(60, 67.5) * mm, "radius": 4 * mm});
            skCircle(sketch, "E79.10", {"center": v(60, -67.5) * mm, "radius": 4 * mm});
            skCircle(sketch, "E79.11", {"center": v(-60, -67.5) * mm, "radius": 4 * mm});
            skArc(sketch, "E79.12", {"start": v(-56.15, -48.18) * mm, "mid": v(0, -67.5) * mm, "end": v(56.15, -48.18) * mm});
            skArc(sketch, "E79.13", {"start": v(-60, -40.3) * mm, "mid": v(-58.99, -44.68) * mm, "end": v(-56.15, -48.18) * mm});
            skLineSegment(sketch, "E79.14", {"start": v(-60, 40.3) * mm, "end": v(-60, -40.3) * mm});
            skArc(sketch, "E79.15", {"start": v(-56.15, 48.18) * mm, "mid": v(-58.99, 44.68) * mm, "end": v(-60, 40.3) * mm});
            skArc(sketch, "E79.16", {"start": v(56.15, 48.18) * mm, "mid": v(0, 67.5) * mm, "end": v(-56.15, 48.18) * mm});
            skArc(sketch, "E79.17", {"start": v(60, 40.3) * mm, "mid": v(58.99, 44.68) * mm, "end": v(56.15, 48.18) * mm});
            skLineSegment(sketch, "E79.18", {"start": v(60, 40.3) * mm, "end": v(60, -40.3) * mm});
            skArc(sketch, "E79.19", {"start": v(56.15, -48.18) * mm, "mid": v(58.99, -44.68) * mm, "end": v(60, -40.3) * mm});
            skPoint(sketch, "E79.20", {"position": v(77.07, 87.07) * mm});
            skLineSegment(sketch, "E80", {"start": v(0, 90) * mm, "end": v(0, 120) * mm, "construction": true});
            skCircle(sketch, "E81", {"center": v(0, 120) * mm, "radius": 6 * mm});
            skLineSegment(sketch, "E82", {"start": v(-14.81, 108) * mm, "end": v(-14.81, 120) * mm});
            skLineSegment(sketch, "E83", {"start": v(15.19, 120) * mm, "end": v(15.19, 108) * mm});
            skArc(sketch, "E84", {"start": v(15.19, 120) * mm, "mid": v(0.19, 135) * mm, "end": v(-14.81, 120) * mm});
            skLineSegment(sketch, "E85", {"start": v(-14.81, 108) * mm, "end": v(-32.81, 90) * mm});
            skLineSegment(sketch, "E86", {"start": v(15.19, 108) * mm, "end": v(33.19, 90) * mm});
            skLineSegment(sketch, "E87", {"start": v(-80, 0) * mm, "end": v(80, 0) * mm, "construction": true});
            skLineSegment(sketch, "E88.MirrorCS", {"start": v(-14.81, -108) * mm, "end": v(-32.81, -90) * mm});
            skLineSegment(sketch, "E89.MirrorCS", {"start": v(-14.81, -108) * mm, "end": v(-14.81, -120) * mm});
            skArc(sketch, "E90.MirrorCS", {"start": v(15.19, -120) * mm, "mid": v(0.19, -135) * mm, "end": v(-14.81, -120) * mm});
            skLineSegment(sketch, "E91.MirrorCS", {"start": v(15.19, -120) * mm, "end": v(15.19, -108) * mm});
            skLineSegment(sketch, "E92.MirrorCS", {"start": v(15.19, -108) * mm, "end": v(33.19, -90) * mm});
            skLineSegment(sketch, "E93.MirrorCS", {"start": v(0, -90) * mm, "end": v(0, -120) * mm, "construction": true});
            skCircle(sketch, "E94.MirrorC", {"center": v(0, -120) * mm, "radius": 6 * mm});
            skLineSegment(sketch, "E95", {"start": v(-32.81, -90) * mm, "end": v(-14.81, -108) * mm});
            skLineSegment(sketch, "E96", {"start": v(15.19, -108) * mm, "end": v(15.19, -120) * mm});
            skSolve(sketch);
        }
        {
            var Q0;
            Q0 = qSketchRegion(id + "F16", true);
            var Q1;
            Q1=makeQuery(id+"F2.opExtrude","CAP_FACE",FACE,{"disambiguationData":[OSD([sQuery(id+"F0.wireOp",EDGE,"E12"),sQuery(id+"F0.wireOp",EDGE,"E13"),sQuery(id+"F0.wireOp",EDGE,"E14"),sQuery(id+"F0.wireOp",EDGE,"E15"),sQuery(id+"F0.wireOp",EDGE,"E17.filletArc"),sQuery(id+"F0.wireOp",EDGE,"E18.filletArc"),sQuery(id+"F0.wireOp",EDGE,"E19.filletArc"),sQuery(id+"F0.wireOp",EDGE,"E20.filletArc"),sQuery(id+"F0.wireOp",EDGE,"E25.0"),sQuery(id+"F0.wireOp",EDGE,"E25.1"),sQuery(id+"F0.wireOp",EDGE,"E25.2"),sQuery(id+"F0.wireOp",EDGE,"E25.3"),sQuery(id+"F0.wireOp",EDGE,"E25.4"),sQuery(id+"F0.wireOp",EDGE,"E25.5"),sQuery(id+"F0.wireOp",EDGE,"E25.6"),sQuery(id+"F0.wireOp",EDGE,"E25.7")])],"isStart":false});
            extrude(context, id + "F17", {"entities" : qUnion([Q0]), "endBound" : BoundingType.UP_TO_SURFACE, "endBoundEntityFace" : qUnion([Q1]), "depth" : 25 * mm});
        }
    });
